# Revit family: Lighting - Luminii - Vest - 1cm Wet - Array
name_source: partatom
category: Lighting Fixtures
units: mm (PartAtom-declared; Revit-internal decimal feet)

## family parameters
Cut with Voids When Loaded = No
Host = Face
Light Source = No
OmniClass Number = 23.80.70.11.14.21
OmniClass Title = Spots and Tracklight Specialties
Part Type = Normal
Room Calculation Point = No
Round Connector Dimension = Use Diameter
Shared = Yes

## types (3) — shared parameters
Apparent Load = 4 VA
Assembly Code = D5020230
C End Caps Width = 3/16"
CCT = 3000K
Current Amps = 50 A
Default Elevation = 0"
Depth = 4 3/4"
Description = Linear Valance Illumination System
Environment = Indoor
Finish = Metal - Luminii - Silver Anodized Aluminum
Frequency = 60 Hz
Has Battery Backup = No
Has Dimming = Yes
Housing Protection Rating = IP20 Dry/IP66 Wet Series
Initial Color Comments = Perfomance based on 3000K Photometric Web File
Instruction Sheet Link = https://www.luminii.com
Keynote = 26 50 00
Lamp = LED
Lamp Life = 5
Lens Material = Plastic - Luminii - Frosted Lens
Load Classification = Lighting
Lumen Output = 400 lm/ft
Manufacturer = Luminii
Model = 367
Mounting Method = Surface Mount
Number of Poles = 1
Operating Temperature = Consult Manufacturer Website for more Information
Phase = 1
Power Factor = 1
Power Source Type = Driver
Product Documentation Link = https://www.luminii.com
Product Name = Vesta 1 CM Wet
Product Page URL = https://www.luminii.com
URL = https://www.luminii.com
Version = 2020 - v1.0a
Voltage = 120 V
Voltage Comments = 120-277V
Warranty URL = https://www.luminii.com
Wattage Comments = 3.8 W
Width = 2 9/16"

## per-type parameters (varying)
| type | C Light Source |
| Vista 1 Cm Wet - 44.5" Length (A) | Lighting - Luminii - Vest - 1cm Wet - Nested Light Source : Vista 1 Cm Wet - 44.5" Length (A) |
| Vista 1 Cm Wet - 66.5" Length (B) | Lighting - Luminii - Vest - 1cm Wet - Nested Light Source : Vista 1 Cm Wet - 66.5" Length (B) |
| Vista 1 Cm Wet - 88.5" Length (C) | Lighting - Luminii - Vest - 1cm Wet - Nested Light Source : Vista 1 Cm Wet - 88.5" Length (C) |

## geometry (parser evidence)
native form markers: Sweep x5
no freeform markers — native parametric forms only
